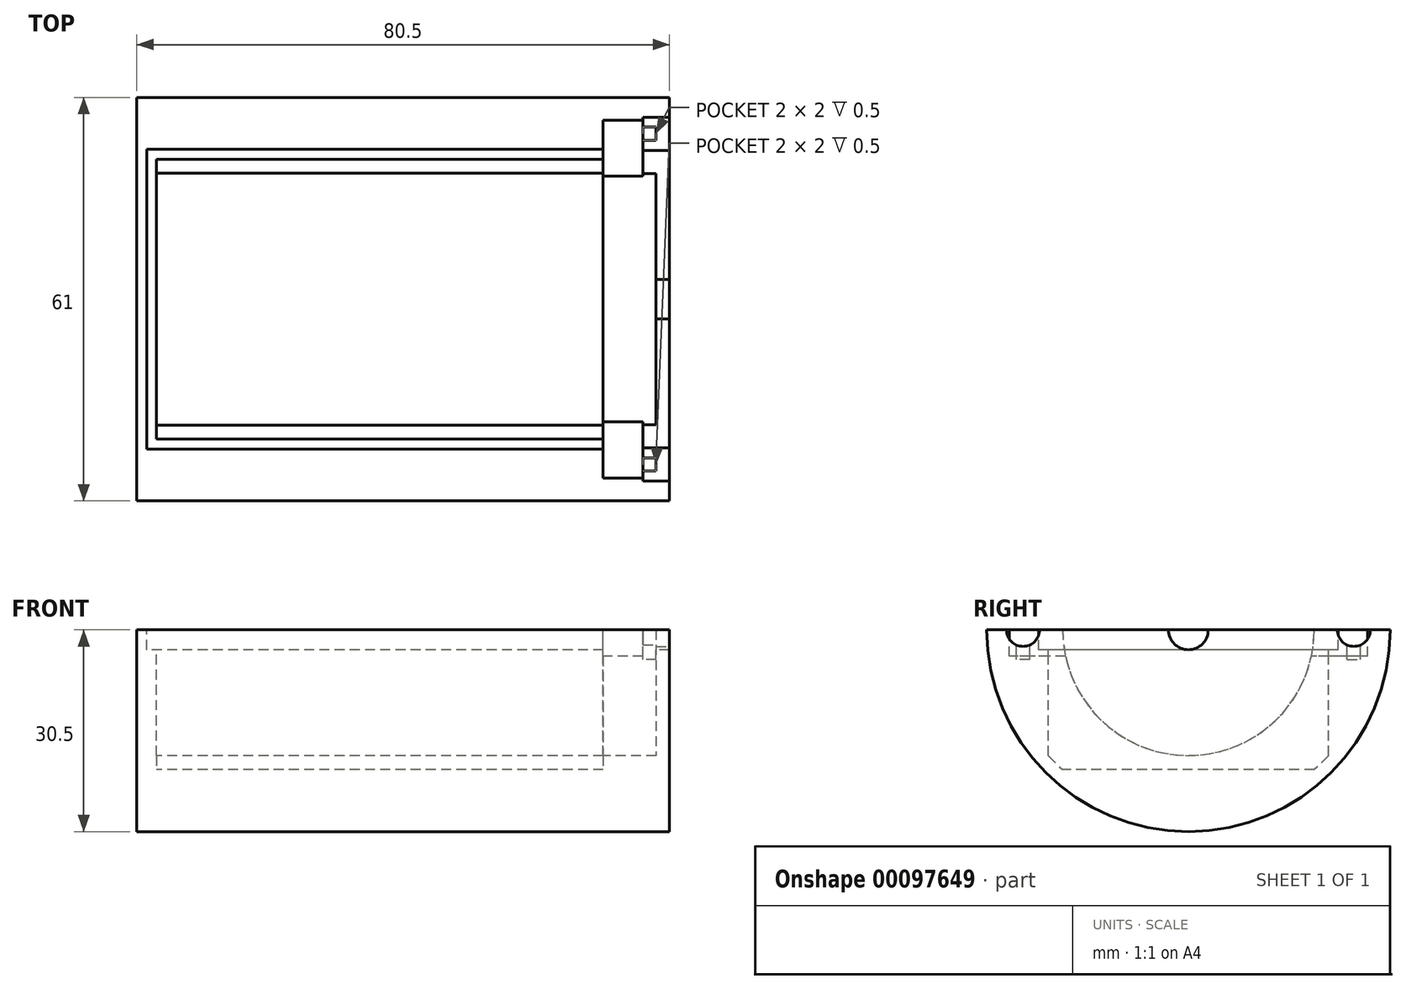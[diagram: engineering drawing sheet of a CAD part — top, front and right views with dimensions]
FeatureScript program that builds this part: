
annotation { "Feature Type Name" : "Feature", "Feature Type Description" : "" }
export const myFeature = defineFeature(function(context is Context, id is Id, definition is map)
    precondition{}
    {
        {
            var Q0;
            Q0=qCreatedBy(makeId("Right.planeOp"),FACE);
            var sketch = newSketch(context, id + "F0", { "sketchPlane" : qUnion([Q0])});
            skArc(sketch, "E0", {"start": v(-30.5, 0) * mm, "mid": v(0, -30.5) * mm, "end": v(30.5, 0) * mm});
            skLineSegment(sketch, "E1.bottom", {"start": v(19.03, -21.15) * mm, "end": v(-19.03, -21.15) * mm});
            skLineSegment(sketch, "E1.left", {"start": v(21.15, -19.03) * mm, "end": v(21.15, 0) * mm});
            skLineSegment(sketch, "E1.right", {"start": v(-21.15, -19.03) * mm, "end": v(-21.15, 0) * mm});
            skLineSegment(sketch, "E2", {"start": v(-30.5, 0) * mm, "end": v(30.5, 0) * mm});
            skPoint(sketch, "E2.endSnap0", {"position": v(21.15, 0) * mm});
            skLineSegment(sketch, "E3", {"start": v(-21.15, -19.03) * mm, "end": v(-19.03, -21.15) * mm});
            skLineSegment(sketch, "E4.MirrorCS", {"start": v(21.15, -19.03) * mm, "end": v(19.03, -21.15) * mm});
            skSolve(sketch);
        }
        {
            var Q0;
            {var subQ0=sQuery(id+"F0.wireOp",EDGE,"E2");var subQ3=sQuery(id+"F0.wireOp",EDGE,"E1.right");var subQ6=makeQuery(id+"F0.imprint","INTERSECT",VERTEX,{"derivedFrom":[subQ3,subQ0]});Q0=makeQuery(id+"F0.imprint","IMPRINT",FACE,{"disambiguationData":[TD([[makeQuery(id+"F0.imprint","IMPRINT",EDGE,{"disambiguationData":[TD([[subQ6,1.0]])],"derivedFrom":subQ3}),1.0]])]});}
            var Q1;
            {var subQ0=sQuery(id+"F0.wireOp",EDGE,"E1.bottom");var subQ5=makeQuery(id+"F0.imprint","INTERSECT",VERTEX,{"derivedFrom":[subQ0,sQuery(id+"F0.wireOp",EDGE,"E3")]});Q1=makeQuery(id+"F0.imprint","IMPRINT",FACE,{"disambiguationData":[TD([[makeQuery(id+"F0.imprint","IMPRINT",EDGE,{"disambiguationData":[TD([[subQ5,1.0]])],"derivedFrom":subQ0}),1.0]])]});}
            var Q2;
            {var subQ0=sQuery(id+"F0.wireOp",EDGE,"E2");var subQ3=sQuery(id+"F0.wireOp",EDGE,"E1.left");var subQ6=makeQuery(id+"F0.imprint","INTERSECT",VERTEX,{"derivedFrom":[subQ3,subQ0]});Q2=makeQuery(id+"F0.imprint","IMPRINT",FACE,{"disambiguationData":[TD([[makeQuery(id+"F0.imprint","IMPRINT",EDGE,{"disambiguationData":[TD([[subQ6,1.0]])],"derivedFrom":subQ3}),-1.0]])]});}
            var Q3;
            {var subQ3=sQuery(id+"F0.wireOp",EDGE,"E4.MirrorCS");Q3=makeQuery(id+"F0.imprint","IMPRINT",FACE,{"disambiguationData":[TD([[makeQuery(id+"F0.imprint","IMPRINT",EDGE,{"derivedFrom":subQ3}),1.0]])]});}
            var Q4;
            {var subQ3=sQuery(id+"F0.wireOp",EDGE,"E3");Q4=makeQuery(id+"F0.imprint","IMPRINT",FACE,{"disambiguationData":[TD([[makeQuery(id+"F0.imprint","IMPRINT",EDGE,{"derivedFrom":subQ3}),-1.0]])]});}
            extrude(context, id + "F1", {"entities" : qUnion([Q0, Q1, Q2, Q3, Q4]), "endBound" : BoundingType.SYMMETRIC, "depth" : 67.5 * mm});
        }
        {
            var Q0;
            Q0=makeQuery(id+"F1.opExtrude","CAP_FACE",FACE,{"disambiguationData":[OSD([sQuery(id+"F0.wireOp",EDGE,"E0"),sQuery(id+"F0.wireOp",EDGE,"E1.bottom"),sQuery(id+"F0.wireOp",EDGE,"E1.left"),sQuery(id+"F0.wireOp",EDGE,"E1.right"),sQuery(id+"F0.wireOp",EDGE,"E2"),sQuery(id+"F0.wireOp",EDGE,"E3"),sQuery(id+"F0.wireOp",EDGE,"E4.MirrorCS")])],"isStart":false});
            var sketch = newSketch(context, id + "F2", { "sketchPlane" : qUnion([Q0])});
            skArc(sketch, "E5", {"start": v(-30.5, 0) * mm, "mid": v(0, -30.5) * mm, "end": v(30.5, 0) * mm});
            skLineSegment(sketch, "E6", {"start": v(-30.5, 0) * mm, "end": v(30.5, 0) * mm});
            skSolve(sketch);
        }
        {
            var Q0;
            Q0=makeQuery(id+"F2.imprint","IMPRINT",FACE,{"disambiguationData":[TD([[makeQuery(id+"F2.imprint","IMPRINT",EDGE,{"derivedFrom":makeQuery(id+"F1.opExtrude","CAP_EDGE",EDGE,{"disambiguationData":[OSD([sQuery(id+"F0.wireOp",EDGE,"E1.bottom")])],"isStart":false})}),-1.0]])]});
            var Q1;
            {var subQ1=sQuery(id+"F2.wireOp",EDGE,"E5");Q1=makeQuery(id+"F2.imprint","IMPRINT",FACE,{"disambiguationData":[TD([[makeQuery(id+"F2.imprint","IMPRINT",EDGE,{"derivedFrom":subQ1}),1.0]])]});}
            extrude(context, id + "F3", {"entities" : qUnion([Q0, Q1]), "operationType" : NewBodyOperationType.ADD, "depth" : 10 * mm});
        }
        {
            var Q0;
            Q0=makeQuery(id+"F1.opExtrude","CAP_FACE",FACE,{"disambiguationData":[OSD([sQuery(id+"F0.wireOp",EDGE,"E0"),sQuery(id+"F0.wireOp",EDGE,"E1.bottom"),sQuery(id+"F0.wireOp",EDGE,"E1.left"),sQuery(id+"F0.wireOp",EDGE,"E1.right"),sQuery(id+"F0.wireOp",EDGE,"E2"),sQuery(id+"F0.wireOp",EDGE,"E3"),sQuery(id+"F0.wireOp",EDGE,"E4.MirrorCS")])],"isStart":true});
            var sketch = newSketch(context, id + "F4", { "sketchPlane" : qUnion([Q0])});
            skArc(sketch, "E7", {"start": v(-30.5, 0) * mm, "mid": v(0, -30.5) * mm, "end": v(30.5, 0) * mm});
            skLineSegment(sketch, "E8", {"start": v(-30.5, 0) * mm, "end": v(30.5, 0) * mm});
            skSolve(sketch);
        }
        {
            var Q0;
            Q0=makeQuery(id+"F4.imprint","IMPRINT",FACE,{"disambiguationData":[TD([[makeQuery(id+"F4.imprint","IMPRINT",EDGE,{"derivedFrom":makeQuery(id+"F1.opExtrude","CAP_EDGE",EDGE,{"disambiguationData":[OSD([sQuery(id+"F0.wireOp",EDGE,"E1.bottom")])],"isStart":true})}),1.0]])]});
            var Q1;
            {var subQ1=sQuery(id+"F4.wireOp",EDGE,"E7");Q1=makeQuery(id+"F4.imprint","IMPRINT",FACE,{"disambiguationData":[TD([[makeQuery(id+"F4.imprint","IMPRINT",EDGE,{"derivedFrom":subQ1}),-1.0]])]});}
            extrude(context, id + "F5", {"entities" : qUnion([Q0, Q1]), "operationType" : NewBodyOperationType.ADD, "depth" : 3 * mm});
        }
        {
            var Q0;
            {var subQ0=sQuery(id+"F0.wireOp",EDGE,"E2");var subQ1=sQuery(id+"F0.wireOp",EDGE,"E0");Q0=makeQuery(id+"F5.boolean.opBoolean","MERGE",FACE,{"derivedFrom":[makeQuery(id+"F3.boolean.opBoolean","MERGE",FACE,{"derivedFrom":[makeQuery(id+"F1.opExtrude","SWEPT_FACE",FACE,{"disambiguationData":[OSD([subQ0]),TDD([makeQuery(id+"F0.imprint","IMPRINT",EDGE,{"disambiguationData":[TD([[makeQuery(id+"F0.imprint","INTERSECT",VERTEX,{"disambiguationData":[OD(0.0)],"derivedFrom":[subQ1,subQ0]}),-1.0]])],"derivedFrom":subQ0})])]}),makeQuery(id+"F1.opExtrude","SWEPT_FACE",FACE,{"disambiguationData":[OSD([subQ0]),TDD([makeQuery(id+"F0.imprint","IMPRINT",EDGE,{"disambiguationData":[TD([[makeQuery(id+"F0.imprint","INTERSECT",VERTEX,{"disambiguationData":[OD(1.0)],"derivedFrom":[subQ1,subQ0]}),1.0]])],"derivedFrom":subQ0})])]}),makeQuery(id+"F3.opExtrude","SWEPT_FACE",FACE,{"disambiguationData":[OSD([sQuery(id+"F2.wireOp",EDGE,"E6")])]})]}),makeQuery(id+"F5.opExtrude","SWEPT_FACE",FACE,{"disambiguationData":[OSD([sQuery(id+"F4.wireOp",EDGE,"E8")])]})]});}
            var sketch = newSketch(context, id + "F6", { "sketchPlane" : qUnion([Q0])});
            skLineSegment(sketch, "E9.bottom", {"start": v(33.75, 0) * mm, "end": v(41.75, 0) * mm});
            skLineSegment(sketch, "E9.top", {"start": v(33.75, 19) * mm, "end": v(41.75, 19) * mm});
            skLineSegment(sketch, "E9.left", {"start": v(33.75, 0) * mm, "end": v(33.75, 19) * mm});
            skLineSegment(sketch, "E9.right", {"start": v(41.75, 0) * mm, "end": v(41.75, 19) * mm});
            skLineSegment(sketch, "E10.bottom", {"start": v(43.75, 0) * mm, "end": v(41.75, 0) * mm});
            skLineSegment(sketch, "E10.top", {"start": v(43.75, 3) * mm, "end": v(41.75, 3) * mm});
            skLineSegment(sketch, "E10.left", {"start": v(43.75, 0) * mm, "end": v(43.75, 3) * mm});
            skLineSegment(sketch, "E10.right", {"start": v(41.75, 0) * mm, "end": v(41.75, 3) * mm});
            skLineSegment(sketch, "E11.bottom", {"start": v(39.75, -22.5) * mm, "end": v(43.75, -22.5) * mm});
            skLineSegment(sketch, "E11.top", {"start": v(39.75, -27.5) * mm, "end": v(43.75, -27.5) * mm});
            skLineSegment(sketch, "E11.left", {"start": v(39.75, -22.5) * mm, "end": v(39.75, -27.5) * mm});
            skLineSegment(sketch, "E11.right", {"start": v(43.75, -22.5) * mm, "end": v(43.75, -27.5) * mm});
            skLineSegment(sketch, "E12.MirrorCS", {"start": v(39.75, 22.5) * mm, "end": v(39.75, 27.5) * mm});
            skLineSegment(sketch, "E13.MirrorCS", {"start": v(39.75, 22.5) * mm, "end": v(43.75, 22.5) * mm});
            skLineSegment(sketch, "E14.MirrorCS", {"start": v(39.75, 27.5) * mm, "end": v(43.75, 27.5) * mm});
            skLineSegment(sketch, "E15.MirrorCS", {"start": v(43.75, 22.5) * mm, "end": v(43.75, 27.5) * mm});
            skLineSegment(sketch, "E16", {"start": v(39.75, -25) * mm, "end": v(43.75, -25) * mm});
            skLineSegment(sketch, "E17.MirrorCS", {"start": v(39.75, 25) * mm, "end": v(43.75, 25) * mm});
            skSolve(sketch);
        }
        {
            var Q0;
            Q0=makeQuery(id+"F6.imprint","IMPRINT",FACE,{"disambiguationData":[TD([[makeQuery(id+"F6.imprint","IMPRINT",EDGE,{"derivedFrom":sQuery(id+"F6.wireOp",EDGE,"E9.bottom")}),1.0]])]});
            var Q1;
            Q1=makeQuery(id+"F6.imprint","IMPRINT",FACE,{"disambiguationData":[TD([[makeQuery(id+"F6.imprint","IMPRINT",EDGE,{"derivedFrom":sQuery(id+"F6.wireOp",EDGE,"E10.bottom")}),-1.0]])]});
            var Q2;
            Q2=sQuery(id+"F6.wireOp",EDGE,"E9.bottom");
            revolve(context, id + "F7", {"operationType" : NewBodyOperationType.REMOVE, "entities" : qUnion([Q0, Q1]), "axis" : qUnion([Q2]), "revolveType" : RevolveType.FULL});
        }
        {
            var Q0;
            {var subQ0=sQuery(id+"F6.wireOp",EDGE,"E11.top");Q0=makeQuery(id+"F6.imprint","IMPRINT",FACE,{"disambiguationData":[TD([[makeQuery(id+"F6.imprint","IMPRINT",EDGE,{"derivedFrom":subQ0}),1.0]])]});}
            var Q1;
            Q1=sQuery(id+"F6.wireOp",EDGE,"E16");
            revolve(context, id + "F8", {"operationType" : NewBodyOperationType.REMOVE, "entities" : qUnion([Q0]), "axis" : qUnion([Q1]), "revolveType" : RevolveType.FULL, "oppositeDirection" : true});
        }
        {
            var Q0;
            {var subQ0=sQuery(id+"F6.wireOp",EDGE,"E13.MirrorCS");Q0=makeQuery(id+"F6.imprint","IMPRINT",FACE,{"disambiguationData":[TD([[makeQuery(id+"F6.imprint","IMPRINT",EDGE,{"derivedFrom":subQ0}),1.0]])]});}
            var Q1;
            Q1=sQuery(id+"F6.wireOp",EDGE,"E17.MirrorCS");
            revolve(context, id + "F9", {"operationType" : NewBodyOperationType.REMOVE, "entities" : qUnion([Q0]), "axis" : qUnion([Q1]), "revolveType" : RevolveType.FULL, "oppositeDirection" : true});
        }
        {
            var Q0;
            {var subQ16=sQuery(id+"F6.wireOp",EDGE,"E9.bottom");Q0=makeQuery(id+"F6.imprint","IMPRINT",FACE,{"disambiguationData":[TD([[makeQuery(id+"F6.imprint","IMPRINT",EDGE,{"derivedFrom":subQ16}),-1.0]])]});}
            var sketch = newSketch(context, id + "F10", { "sketchPlane" : qUnion([Q0])});
            skLineSegment(sketch, "E18.bottom", {"start": v(41.75, -26) * mm, "end": v(39.75, -26) * mm});
            skLineSegment(sketch, "E18.top", {"start": v(41.75, -24) * mm, "end": v(39.75, -24) * mm});
            skLineSegment(sketch, "E18.left", {"start": v(41.75, -26) * mm, "end": v(41.75, -24) * mm});
            skPoint(sketch, "E18.middle", {"position": v(39.75, -25) * mm});
            skLineSegment(sketch, "E19", {"start": v(39.75, -24) * mm, "end": v(39.75, -26) * mm});
            skPoint(sketch, "E18.right.end.orphan", {"position": v(37.75, -24) * mm});
            skPoint(sketch, "E20.orphan", {"position": v(37.75, -26) * mm});
            skLineSegment(sketch, "E21.MirrorCS", {"start": v(41.75, 24) * mm, "end": v(39.75, 24) * mm});
            skLineSegment(sketch, "E22.MirrorCS", {"start": v(41.75, 26) * mm, "end": v(41.75, 24) * mm});
            skLineSegment(sketch, "E23.MirrorCS", {"start": v(41.75, 26) * mm, "end": v(39.75, 26) * mm});
            skLineSegment(sketch, "E24.MirrorCS", {"start": v(39.75, 24) * mm, "end": v(39.75, 26) * mm});
            skSolve(sketch);
        }
        {
            var Q0;
            {var subQ5=sQuery(id+"F10.wireOp",EDGE,"E18.bottom");Q0=makeQuery(id+"F10.imprint","IMPRINT",FACE,{"disambiguationData":[TD([[makeQuery(id+"F10.imprint","IMPRINT",EDGE,{"derivedFrom":subQ5}),-1.0]])]});}
            var Q1;
            {var subQ2=sQuery(id+"F10.wireOp",EDGE,"E21.MirrorCS");Q1=makeQuery(id+"F10.imprint","IMPRINT",FACE,{"disambiguationData":[TD([[makeQuery(id+"F10.imprint","IMPRINT",EDGE,{"derivedFrom":subQ2}),-1.0]])]});}
            extrude(context, id + "F11", {"entities" : qUnion([Q0, Q1]), "operationType" : NewBodyOperationType.REMOVE, "oppositeDirection" : true, "depth" : 4.5 * mm});
        }
        {
            var Q0;
            {var subQ0=sQuery(id+"F0.wireOp",EDGE,"E2");var subQ1=sQuery(id+"F0.wireOp",EDGE,"E0");Q0=makeQuery(id+"F5.boolean.opBoolean","MERGE",FACE,{"derivedFrom":[makeQuery(id+"F3.boolean.opBoolean","MERGE",FACE,{"derivedFrom":[makeQuery(id+"F1.opExtrude","SWEPT_FACE",FACE,{"disambiguationData":[OSD([subQ0]),TDD([makeQuery(id+"F0.imprint","IMPRINT",EDGE,{"disambiguationData":[TD([[makeQuery(id+"F0.imprint","INTERSECT",VERTEX,{"disambiguationData":[OD(0.0)],"derivedFrom":[subQ1,subQ0]}),-1.0]])],"derivedFrom":subQ0})])]}),makeQuery(id+"F1.opExtrude","SWEPT_FACE",FACE,{"disambiguationData":[OSD([subQ0]),TDD([makeQuery(id+"F0.imprint","IMPRINT",EDGE,{"disambiguationData":[TD([[makeQuery(id+"F0.imprint","INTERSECT",VERTEX,{"disambiguationData":[OD(1.0)],"derivedFrom":[subQ1,subQ0]}),1.0]])],"derivedFrom":subQ0})])]}),makeQuery(id+"F3.opExtrude","SWEPT_FACE",FACE,{"disambiguationData":[OSD([sQuery(id+"F2.wireOp",EDGE,"E6")])]})]}),makeQuery(id+"F5.opExtrude","SWEPT_FACE",FACE,{"disambiguationData":[OSD([sQuery(id+"F4.wireOp",EDGE,"E8")])]})]});}
            var sketch = newSketch(context, id + "F12", { "sketchPlane" : qUnion([Q0])});
            skLineSegment(sketch, "E25.bottom", {"start": v(33.75, 27.06) * mm, "end": v(39.75, 27.06) * mm});
            skLineSegment(sketch, "E25.top", {"start": v(33.75, -27.06) * mm, "end": v(39.75, -27.06) * mm});
            skLineSegment(sketch, "E25.left", {"start": v(33.75, 27.06) * mm, "end": v(33.75, -27.06) * mm});
            skLineSegment(sketch, "E25.right", {"start": v(39.75, 27.06) * mm, "end": v(39.75, -27.06) * mm});
            skPoint(sketch, "E26", {"position": v(36.75, 24.06) * mm});
            skPoint(sketch, "E27.MirrorP", {"position": v(36.75, -24.06) * mm});
            skSolve(sketch);
        }
        {
            var Q0;
            {var subQ7=sQuery(id+"F12.wireOp",EDGE,"E25.bottom");Q0=makeQuery(id+"F12.imprint","IMPRINT",FACE,{"disambiguationData":[TD([[makeQuery(id+"F12.imprint","IMPRINT",EDGE,{"derivedFrom":subQ7}),-1.0]])]});}
            var Q1;
            {var subQ4=sQuery(id+"F12.wireOp",EDGE,"E25.top");Q1=makeQuery(id+"F12.imprint","IMPRINT",FACE,{"disambiguationData":[TD([[makeQuery(id+"F12.imprint","IMPRINT",EDGE,{"derivedFrom":subQ4}),1.0]])]});}
            var Q2;
            {var subQ0=sQuery(id+"F12.wireOp",EDGE,"E25.left");var subQ1=makeQuery(id+"F7.opRevolve","SWEPT_FACE",FACE,{"disambiguationData":[OSD([sQuery(id+"F6.wireOp",EDGE,"E9.top")])]});var subQ2=sQuery(id+"F0.wireOp",EDGE,"E2");var subQ3=sQuery(id+"F0.wireOp",EDGE,"E0");var subQ4=makeQuery(id+"F5.boolean.opBoolean","MERGE",FACE,{"derivedFrom":[makeQuery(id+"F3.boolean.opBoolean","MERGE",FACE,{"derivedFrom":[makeQuery(id+"F1.opExtrude","SWEPT_FACE",FACE,{"disambiguationData":[OSD([subQ2]),TDD([makeQuery(id+"F0.imprint","IMPRINT",EDGE,{"disambiguationData":[TD([[makeQuery(id+"F0.imprint","INTERSECT",VERTEX,{"disambiguationData":[OD(0.0)],"derivedFrom":[subQ3,subQ2]}),-1.0]])],"derivedFrom":subQ2})])]}),makeQuery(id+"F1.opExtrude","SWEPT_FACE",FACE,{"disambiguationData":[OSD([subQ2]),TDD([makeQuery(id+"F0.imprint","IMPRINT",EDGE,{"disambiguationData":[TD([[makeQuery(id+"F0.imprint","INTERSECT",VERTEX,{"disambiguationData":[OD(1.0)],"derivedFrom":[subQ3,subQ2]}),1.0]])],"derivedFrom":subQ2})])]}),makeQuery(id+"F3.opExtrude","SWEPT_FACE",FACE,{"disambiguationData":[OSD([sQuery(id+"F2.wireOp",EDGE,"E6")])]})]}),makeQuery(id+"F5.opExtrude","SWEPT_FACE",FACE,{"disambiguationData":[OSD([sQuery(id+"F4.wireOp",EDGE,"E8")])]})]});var subQ5=makeQuery(id+"F7.boolean.opBoolean","INTERSECT",EDGE,{"disambiguationData":[OD(0.0)],"derivedFrom":[subQ4,subQ1]});var subQ6=makeQuery(id+"F12.imprint","INTERSECT",VERTEX,{"derivedFrom":[subQ5,subQ0]});var subQ7=makeQuery(id+"F7.boolean.opBoolean","INTERSECT",EDGE,{"disambiguationData":[OD(1.0)],"derivedFrom":[subQ4,subQ1]});var subQ8=makeQuery(id+"F12.imprint","INTERSECT",VERTEX,{"derivedFrom":[subQ7,subQ0]});Q2=makeQuery(id+"F12.imprint","IMPRINT",FACE,{"disambiguationData":[TD([[makeQuery(id+"F12.imprint","IMPRINT",EDGE,{"disambiguationData":[TD([[subQ6,-1.0],[subQ8,1.0]])],"derivedFrom":subQ0}),1.0]])]});}
            extrude(context, id + "F13", {"entities" : qUnion([Q0, Q1, Q2]), "operationType" : NewBodyOperationType.REMOVE, "oppositeDirection" : true, "depth" : 4 * mm});
        }
        {
            var Q0;
            {var subQ0=sQuery(id+"F4.wireOp",EDGE,"E8");var subQ1=sQuery(id+"F4.wireOp",EDGE,"E7");var subQ2=sQuery(id+"F2.wireOp",EDGE,"E6");var subQ3=sQuery(id+"F2.wireOp",EDGE,"E5");var subQ4=sQuery(id+"F0.wireOp",EDGE,"E0");var subQ5=sQuery(id+"F0.wireOp",EDGE,"E1.left");var subQ6=sQuery(id+"F0.wireOp",EDGE,"E1.right");var subQ7=sQuery(id+"F0.wireOp",EDGE,"E2");Q0=makeQuery(id+"F13.boolean.opBoolean","SPLIT",FACE,{"disambiguationData":[TD([makeQuery(id+"F1.opExtrude","SWEPT_FACE",FACE,{"disambiguationData":[OSD([subQ4])]}),makeQuery(id+"F1.opExtrude","SWEPT_FACE",FACE,{"disambiguationData":[OSD([subQ5])]}),makeQuery(id+"F1.opExtrude","SWEPT_FACE",FACE,{"disambiguationData":[OSD([subQ6])]}),makeQuery(id+"F3.opExtrude","SWEPT_FACE",FACE,{"disambiguationData":[OSD([subQ3])]}),makeQuery(id+"F3.opExtrude","CAP_FACE",FACE,{"disambiguationData":[OSD([subQ3,subQ2])],"isStart":false}),makeQuery(id+"F5.opExtrude","SWEPT_FACE",FACE,{"disambiguationData":[OSD([subQ1])]}),makeQuery(id+"F5.opExtrude","CAP_FACE",FACE,{"disambiguationData":[OSD([subQ1,subQ0])],"isStart":true}),makeQuery(id+"F5.opExtrude","CAP_FACE",FACE,{"disambiguationData":[OSD([subQ1,subQ0])],"isStart":false}),makeQuery(id+"F8.boolean.opBoolean","COPY",FACE,{"derivedFrom":makeQuery(id+"F8.opRevolve","SWEPT_FACE",FACE,{"disambiguationData":[OSD([sQuery(id+"F6.wireOp",EDGE,"E11.top")])]})}),makeQuery(id+"F8.boolean.opBoolean","COPY",FACE,{"derivedFrom":makeQuery(id+"F8.opRevolve","SWEPT_FACE",FACE,{"disambiguationData":[OSD([sQuery(id+"F6.wireOp",EDGE,"E11.left")])]})}),makeQuery(id+"F9.boolean.opBoolean","COPY",FACE,{"derivedFrom":makeQuery(id+"F9.opRevolve","SWEPT_FACE",FACE,{"disambiguationData":[OSD([sQuery(id+"F6.wireOp",EDGE,"E12.MirrorCS")])]})}),makeQuery(id+"F9.boolean.opBoolean","COPY",FACE,{"derivedFrom":makeQuery(id+"F9.opRevolve","SWEPT_FACE",FACE,{"disambiguationData":[OSD([sQuery(id+"F6.wireOp",EDGE,"E13.MirrorCS")])]})}),makeQuery(id+"F11.opExtrude","SWEPT_FACE",FACE,{"disambiguationData":[OSD([sQuery(id+"F10.wireOp",EDGE,"E19")])]}),makeQuery(id+"F11.opExtrude","SWEPT_FACE",FACE,{"disambiguationData":[OSD([sQuery(id+"F10.wireOp",EDGE,"E24.MirrorCS")])]}),makeQuery(id+"F13.opExtrude","SWEPT_FACE",FACE,{"disambiguationData":[OSD([sQuery(id+"F12.wireOp",EDGE,"E25.bottom")])]}),makeQuery(id+"F13.opExtrude","SWEPT_FACE",FACE,{"disambiguationData":[OSD([sQuery(id+"F12.wireOp",EDGE,"E25.top")])]}),makeQuery(id+"F13.opExtrude","SWEPT_FACE",FACE,{"disambiguationData":[OSD([sQuery(id+"F12.wireOp",EDGE,"E25.left")])]})])],"derivedFrom":makeQuery(id+"F5.boolean.opBoolean","MERGE",FACE,{"derivedFrom":[makeQuery(id+"F3.boolean.opBoolean","MERGE",FACE,{"derivedFrom":[makeQuery(id+"F1.opExtrude","SWEPT_FACE",FACE,{"disambiguationData":[OSD([subQ7]),TDD([makeQuery(id+"F0.imprint","IMPRINT",EDGE,{"disambiguationData":[TD([[makeQuery(id+"F0.imprint","INTERSECT",VERTEX,{"disambiguationData":[OD(0.0)],"derivedFrom":[subQ4,subQ7]}),-1.0]])],"derivedFrom":subQ7})])]}),makeQuery(id+"F1.opExtrude","SWEPT_FACE",FACE,{"disambiguationData":[OSD([subQ7]),TDD([makeQuery(id+"F0.imprint","IMPRINT",EDGE,{"disambiguationData":[TD([[makeQuery(id+"F0.imprint","INTERSECT",VERTEX,{"disambiguationData":[OD(1.0)],"derivedFrom":[subQ4,subQ7]}),1.0]])],"derivedFrom":subQ7})])]}),makeQuery(id+"F3.opExtrude","SWEPT_FACE",FACE,{"disambiguationData":[OSD([subQ2])]})]}),makeQuery(id+"F5.opExtrude","SWEPT_FACE",FACE,{"disambiguationData":[OSD([subQ0])]})]})});}
            var sketch = newSketch(context, id + "F14", { "sketchPlane" : qUnion([Q0])});
            skLineSegment(sketch, "E28.bottom", {"start": v(33.75, 21.15) * mm, "end": v(-33.75, 21.15) * mm});
            skLineSegment(sketch, "E28.top", {"start": v(33.75, 22.65) * mm, "end": v(-33.75, 22.65) * mm});
            skLineSegment(sketch, "E28.left", {"start": v(33.75, 21.15) * mm, "end": v(33.75, 22.65) * mm});
            skLineSegment(sketch, "E28.right", {"start": v(-33.75, 21.15) * mm, "end": v(-33.75, 22.65) * mm});
            skPoint(sketch, "E29.oppositeSnap0", {"position": v(-36.75, 0) * mm});
            skLineSegment(sketch, "E29.bottom", {"start": v(-33.75, 22.65) * mm, "end": v(-35.25, 22.65) * mm});
            skLineSegment(sketch, "E29.top", {"start": v(-33.75, 0) * mm, "end": v(-35.25, 0) * mm});
            skLineSegment(sketch, "E29.left", {"start": v(-33.75, 22.65) * mm, "end": v(-33.75, 0) * mm});
            skLineSegment(sketch, "E29.right", {"start": v(-35.25, 22.65) * mm, "end": v(-35.25, 0) * mm});
            skLineSegment(sketch, "E30.MirrorCS", {"start": v(33.75, -22.65) * mm, "end": v(-33.75, -22.65) * mm});
            skLineSegment(sketch, "E31.MirrorCS", {"start": v(33.75, -21.15) * mm, "end": v(-33.75, -21.15) * mm});
            skLineSegment(sketch, "E32.MirrorCS", {"start": v(33.75, -21.15) * mm, "end": v(33.75, -22.65) * mm});
            skLineSegment(sketch, "E33.MirrorCS", {"start": v(-33.75, -22.65) * mm, "end": v(-33.75, 0) * mm});
            skLineSegment(sketch, "E34.MirrorCS", {"start": v(-35.25, -22.65) * mm, "end": v(-35.25, 0) * mm});
            skLineSegment(sketch, "E35.MirrorCS", {"start": v(-33.75, -22.65) * mm, "end": v(-35.25, -22.65) * mm});
            skSolve(sketch);
        }
        {
            var Q0;
            {var subQ0=sQuery(id+"F14.wireOp",EDGE,"E28.bottom");Q0=makeQuery(id+"F14.imprint","IMPRINT",FACE,{"disambiguationData":[TD([[makeQuery(id+"F14.imprint","IMPRINT",EDGE,{"derivedFrom":subQ0}),-1.0]])]});}
            var Q1;
            {var subQ0=sQuery(id+"F14.wireOp",EDGE,"E30.MirrorCS");Q1=makeQuery(id+"F14.imprint","IMPRINT",FACE,{"disambiguationData":[TD([[makeQuery(id+"F14.imprint","IMPRINT",EDGE,{"derivedFrom":subQ0}),-1.0]])]});}
            var Q2;
            {var subQ2=sQuery(id+"F14.wireOp",EDGE,"E29.bottom");Q2=makeQuery(id+"F14.imprint","IMPRINT",FACE,{"disambiguationData":[TD([[makeQuery(id+"F14.imprint","IMPRINT",EDGE,{"derivedFrom":subQ2}),1.0]])]});}
            var Q3;
            Q3=makeQuery(id+"F14.imprint","IMPRINT",FACE,{"disambiguationData":[TD([[makeQuery(id+"F14.imprint","IMPRINT",EDGE,{"derivedFrom":sQuery(id+"F14.wireOp",EDGE,"E34.MirrorCS")}),-1.0]])]});
            extrude(context, id + "F15", {"entities" : qUnion([Q0, Q1, Q2, Q3]), "operationType" : NewBodyOperationType.REMOVE, "oppositeDirection" : true, "depth" : 3 * mm});
        }
    });
